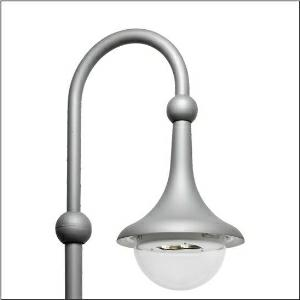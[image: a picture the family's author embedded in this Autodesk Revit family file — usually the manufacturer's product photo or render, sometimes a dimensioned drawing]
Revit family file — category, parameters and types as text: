
# Revit family: grosse_glocke_iq___p1_0a_5xa1565f1f108_f8af
name_source: partatom
category: Lighting Fixtures
units: mm (PartAtom-declared; Revit-internal decimal feet)

## family parameters
Cut with Voids When Loaded = No
Host = Face
Light Source = No
Part Type = Normal
Room Calculation Point = No
Round Connector Dimension = Use Diameter
Shared = No

## types (1)
- --- (1 x LED, 5070 lm, 34.3 W, 3000K)
    Apparent Load = 34 VA
    CIE Flux Codes = 26 57 90 99 100
    Color Rendering = 70
    Color Temperature = 3000K
    Default Elevation = 1800 mm
    Description = Large Bell iQ, mast luminaire, primary light control with 3 zone facetted reflector, of plastic, silver coated, primary optical cover: enclosure, of PMMA, transparent, light distribution: P1.0a, light emission: direct distribution, primary light characteristic: asymmetric, installation type: suspended mounting, High Power LED, rated luminous flux: 5.070lm, luminous efficacy: 148lm/W, light colour: 730, colour temperature: 3000K, control gear: iQ Street-Remote, control: optimised constant luminous flux control (CLO 2.0), Desk-Remote (wireless, voltage-free reading and setting of iQ features in the workshop via application-optimized NFC function/RFID function), Light-Fading, Smart-Wire, Night-Set, Lumen-Switch, Temp-Guard, Auto-Match, Street-Remote, pre-setting: logarithmic dimming characteristic, mains connection: 230..240V, AC, 50/60Hz, start of lifetime: 34W, end of service life: 38W, reduction: 16W, luminaire housing, bell-shaped, of glass-fibre reinforced polyester, coated, Siteco® metallic grey (DB 702S), please order curved mast extension separately, diameter: 530mm, height: 695mm, mounting height: 4..6m, protection rating (complete): IP54, insulation class (complete): insulation class II (safety insulation), certification: CE, ENEC, VDE, impact resistance: IK08, standard-compliant lighting for roads and squares, packaging unit: 1 piece

Light Distribution: P1.0a
    Height = 695 mm
    Lamp = 1 x LED
    Lamp Light Flux = 5070 lm
    Lamp Power = 34.3 W
    Lamp count = 1
    Length = 530 mm
    Luminous efficacy = 148 lm/W
    Manufacturer = Siteco
    ModVariant = No
    Model = 5XA1565F1F108
    Number of Poles = 1
    OnlyDefault = Yes
    Power Factor = 1
    Product Name = Große Glocke iQ | P1.0a
    Product group = mast luminaire | pylon annexe
    ProductGroupID = 6200
    Protection Class = Protection class II
    Protection Degree = IP 54
    RLX_Detail_Level = 1
    RLX_Emergency_Light_Flux = 0 lm
    RLX_Emergency_Type = 0
    RLX_Emergency_Type_DB = No
    RlxData = <blob elided: 53249 chars, md5=bf24bfed>
    Socket = socket
    Standby Power = 0 W
    System Light Flux = 5070 lm
    System Power = 34 W
    Type Comments = factory setting: luminous flux: 100 % | dim-lin: 254 | 640 mA
    Type Image = l_1347688.jpg
    URL = http://relux.com
    VarID = @adj_079601
    Voltage = 0 V
    Weight = 0.00 kg
    Width = 0 mm  [stored 0 ft]

note: [stored X ft] marks values corroborated as IEEE doubles in the binary element streams (Revit-internal decimal feet)

## geometry (parser evidence)
native form markers: Blend x4, Sweep x11
no freeform markers — native parametric forms only
